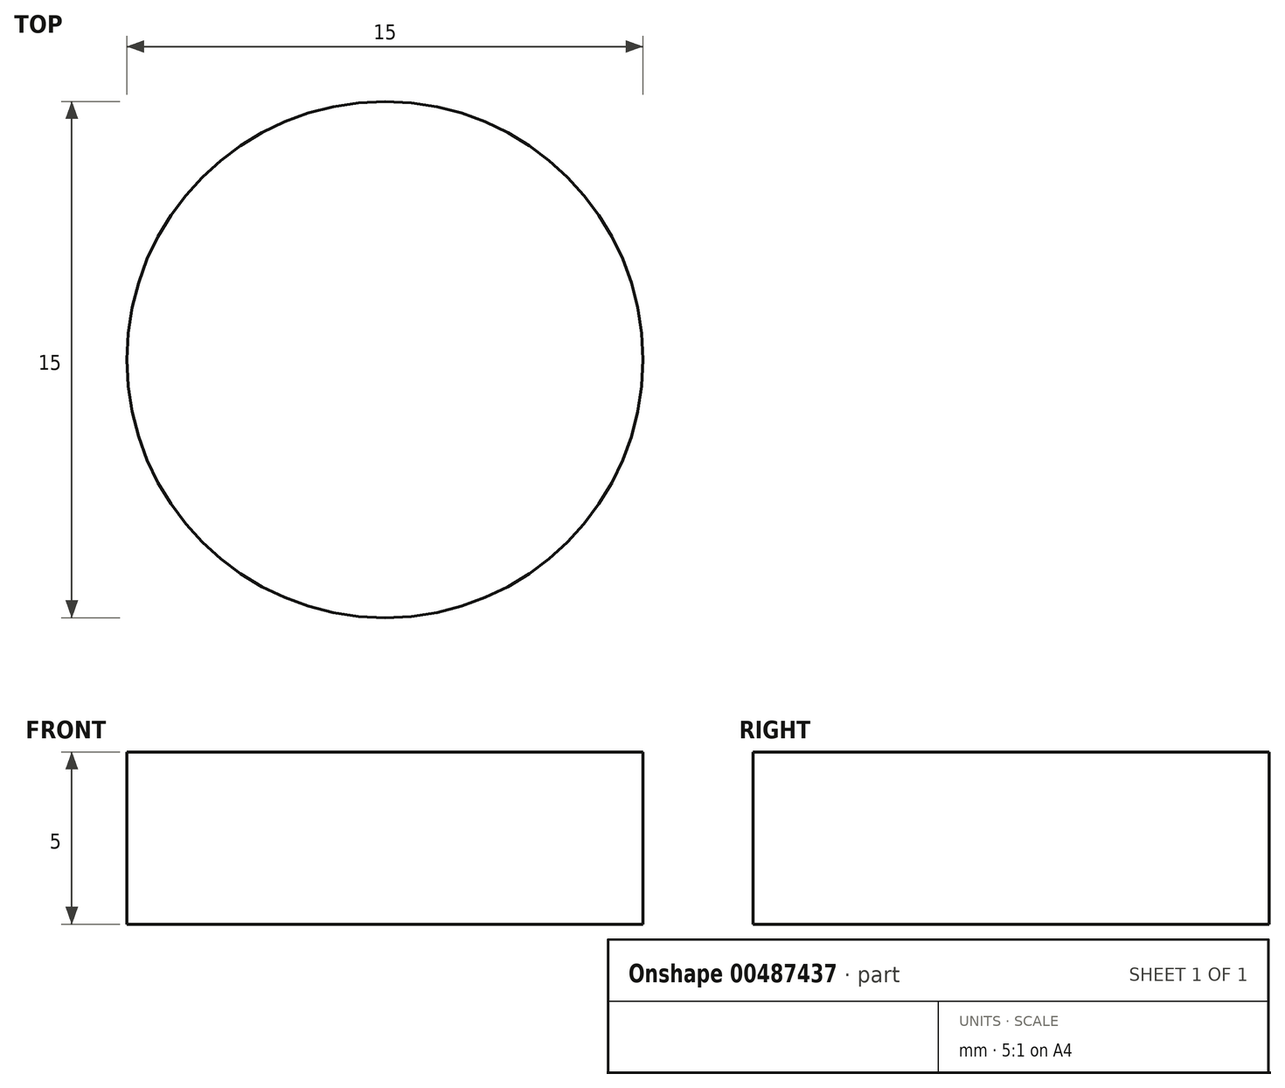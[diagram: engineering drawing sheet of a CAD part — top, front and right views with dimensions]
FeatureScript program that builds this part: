
annotation { "Feature Type Name" : "Feature", "Feature Type Description" : "" }
export const myFeature = defineFeature(function(context is Context, id is Id, definition is map)
    precondition{}
    {
        {
            var Q0;
            Q0=qCreatedBy(makeId("Top.planeOp"),FACE);
            var sketch = newSketch(context, id + "F0", { "sketchPlane" : qUnion([Q0])});
            skCircle(sketch, "E0", {"center": v(0, 0) * mm, "radius": 7.5 * mm});
            skSolve(sketch);
        }
        {
            var Q0;
            Q0=makeQuery(id+"F0.imprint","IMPRINT",FACE,{"disambiguationData":[TD([[makeQuery(id+"F0.imprint","IMPRINT",EDGE,{"derivedFrom":sQuery(id+"F0.wireOp",EDGE,"E0")}),1.0]])]});
            var Q1;
            Q1=sQuery(id+"F0.wireOp",EDGE,"E0");
            extrude(context, id + "F1", {"entities" : qUnion([Q0]), "surfaceEntities" : qUnion([Q1]), "endBound" : BoundingType.SYMMETRIC, "depth" : 5 * mm});
        }
    });
